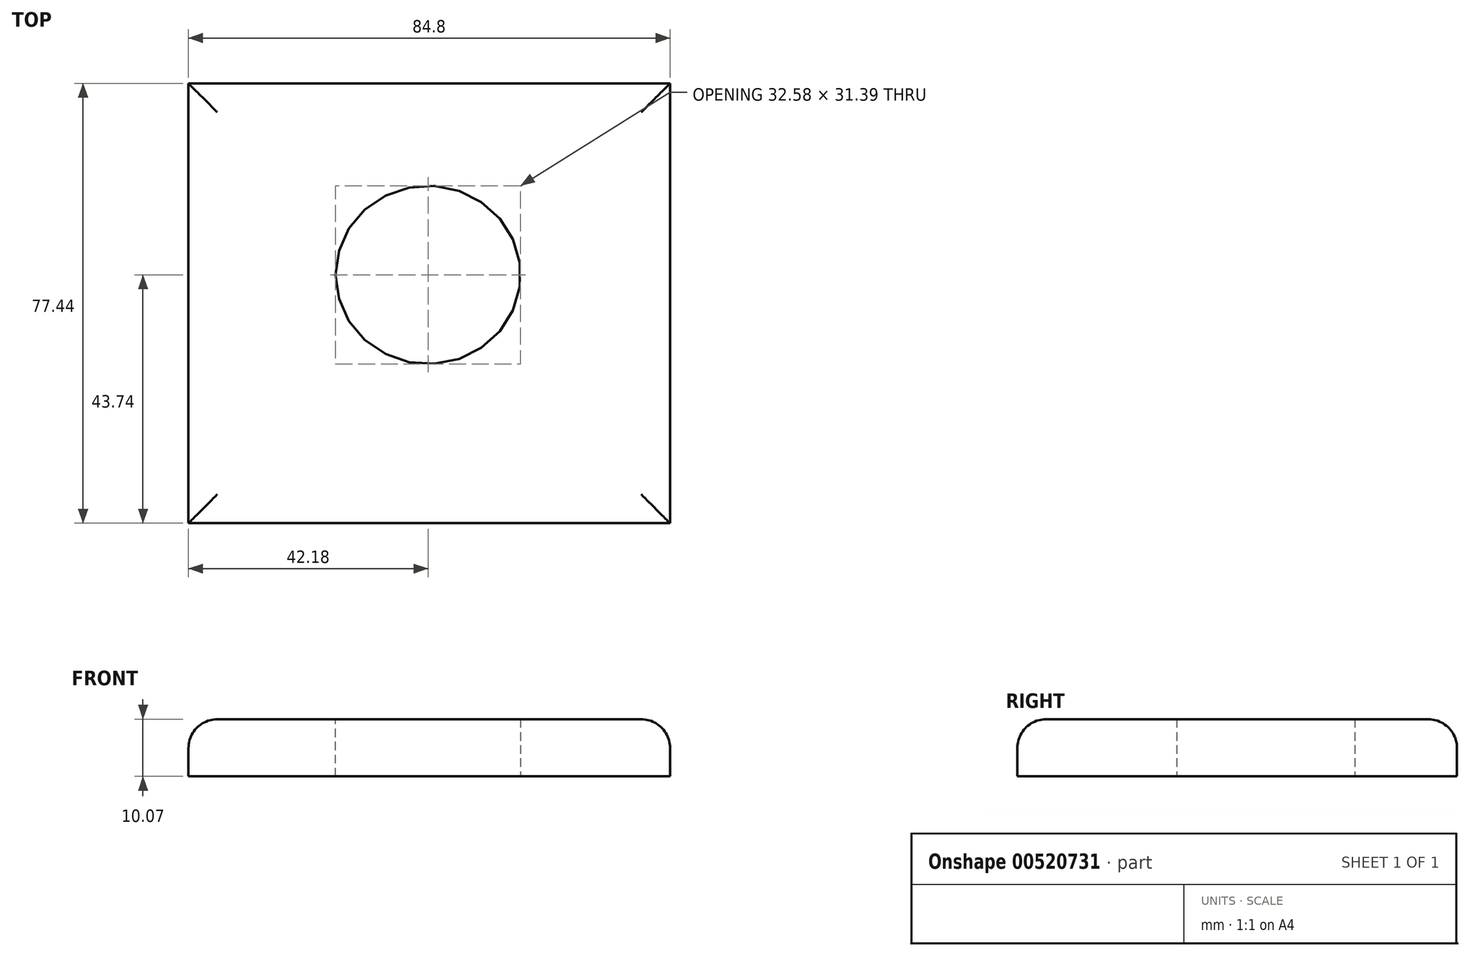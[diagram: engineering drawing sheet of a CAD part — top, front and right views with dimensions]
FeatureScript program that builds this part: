
annotation { "Feature Type Name" : "Feature", "Feature Type Description" : "" }
export const myFeature = defineFeature(function(context is Context, id is Id, definition is map)
    precondition{}
    {
        {
            var Q0;
            Q0=qCreatedBy(makeId("Top.planeOp"),FACE);
            var sketch = newSketch(context, id + "F0", { "sketchPlane" : qUnion([Q0])});
            skLineSegment(sketch, "E0.bottom", {"start": v(-42.18, 51.09) * mm, "end": v(42.62, 51.09) * mm});
            skLineSegment(sketch, "E0.top", {"start": v(-42.18, -26.35) * mm, "end": v(42.62, -26.35) * mm});
            skLineSegment(sketch, "E0.left", {"start": v(-42.18, 51.09) * mm, "end": v(-42.18, -26.35) * mm});
            skLineSegment(sketch, "E0.right", {"start": v(42.62, 51.09) * mm, "end": v(42.62, -26.35) * mm});
            skSolve(sketch);
        }
        {
            var Q0;
            Q0 = qSketchRegion(id + "F0", true);
            extrude(context, id + "F1", {"entities" : qUnion([Q0]), "depth" : 10.07 * mm, "offsetDistance" : 25.4 * mm});
        }
        {
            var Q0;
            Q0=makeQuery(id+"F1.opExtrude","CAP_FACE",FACE,{"disambiguationData":[OSD([sQuery(id+"F0.wireOp",EDGE,"E0.bottom"),sQuery(id+"F0.wireOp",EDGE,"E0.top"),sQuery(id+"F0.wireOp",EDGE,"E0.left"),sQuery(id+"F0.wireOp",EDGE,"E0.right")])],"isStart":false});
            var sketch = newSketch(context, id + "F2", { "sketchPlane" : qUnion([Q0])});
            skEllipse(sketch, "E1", {"center": v(0, 17.39) * mm, "majorRadius": 16.3 * mm, "minorRadius": 15.7 * mm, "majorAxis": v(-1, 0)});
            skSolve(sketch);
        }
        {
            var Q0;
            Q0 = qSketchRegion(id + "F2", true);
            extrude(context, id + "F3", {"entities" : qUnion([Q0]), "operationType" : NewBodyOperationType.REMOVE, "oppositeDirection" : true, "depth" : 86.08 * mm, "offsetDistance" : 25.4 * mm});
        }
        {
            var Q0;
            Q0=makeQuery(id+"F1.opExtrude","CAP_EDGE",EDGE,{"disambiguationData":[OSD([sQuery(id+"F0.wireOp",EDGE,"E0.left")])],"isStart":false});
            var Q1;
            Q1=makeQuery(id+"F1.opExtrude","CAP_EDGE",EDGE,{"disambiguationData":[OSD([sQuery(id+"F0.wireOp",EDGE,"E0.bottom")])],"isStart":false});
            var Q2;
            Q2=makeQuery(id+"F1.opExtrude","CAP_EDGE",EDGE,{"disambiguationData":[OSD([sQuery(id+"F0.wireOp",EDGE,"E0.top")])],"isStart":false});
            var Q3;
            Q3=makeQuery(id+"F1.opExtrude","CAP_EDGE",EDGE,{"disambiguationData":[OSD([sQuery(id+"F0.wireOp",EDGE,"E0.right")])],"isStart":false});
            var Q4;
            Q4=makeQuery(id+"F3.boolean.opBoolean","COPY",EDGE,{"derivedFrom":makeQuery(id+"F3.opExtrude","CAP_EDGE",EDGE,{"disambiguationData":[OSD([sQuery(id+"F2.wireOp",EDGE,"E1")])],"isStart":true})});
            fillet(context, id + "F4", {"entities" : qUnion([Q0, Q1, Q2, Q3, Q4]), "radius" : 5.08 * mm, "tangentPropagation" : true, "allowEdgeOverflow" : false});
        }
    });
